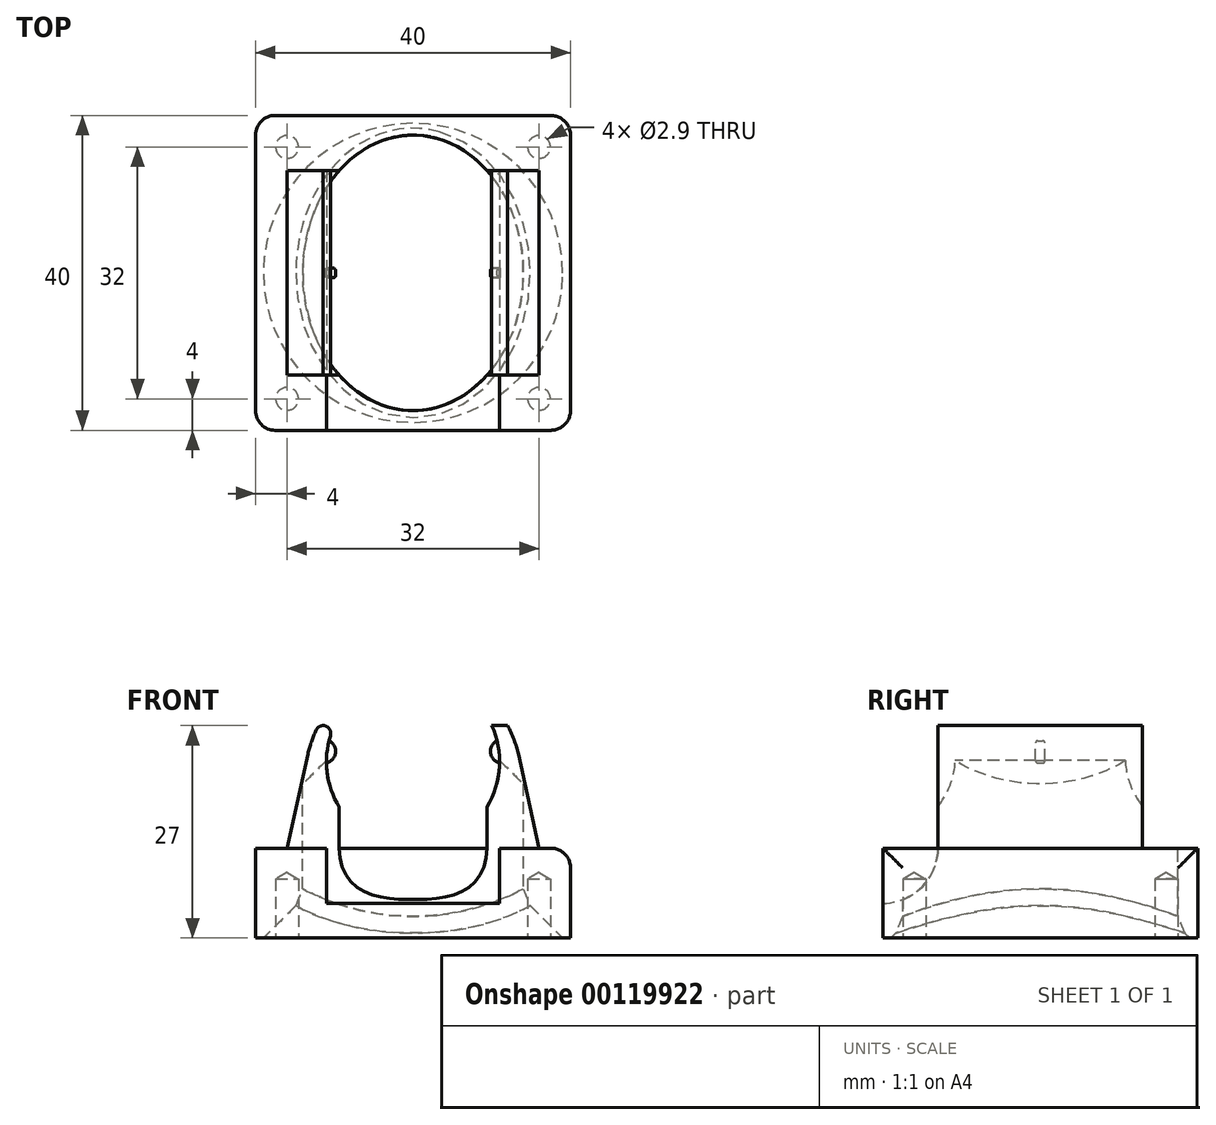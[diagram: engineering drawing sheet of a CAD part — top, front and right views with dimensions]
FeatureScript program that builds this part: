
annotation { "Feature Type Name" : "Feature", "Feature Type Description" : "" }
export const myFeature = defineFeature(function(context is Context, id is Id, definition is map)
    precondition{}
    {
        {
            var Q0;
            Q0=qCreatedBy(makeId("Top.planeOp"),FACE);
            var sketch = newSketch(context, id + "F0", { "sketchPlane" : qUnion([Q0])});
            skLineSegment(sketch, "E0.bottom", {"start": v(20, 20) * mm, "end": v(-20, 20) * mm});
            skLineSegment(sketch, "E0.top", {"start": v(20, -20) * mm, "end": v(-20, -20) * mm});
            skLineSegment(sketch, "E0.left", {"start": v(20, 20) * mm, "end": v(20, -20) * mm});
            skLineSegment(sketch, "E0.right", {"start": v(-20, 20) * mm, "end": v(-20, -20) * mm});
            skPoint(sketch, "E0.middle", {"position": v(0, 0) * mm});
            skSolve(sketch);
        }
        {
            var Q0;
            Q0 = qSketchRegion(id + "F0", true);
            extrude(context, id + "F1", {"entities" : qUnion([Q0]), "depth" : 27 * mm});
        }
        {
            var Q0;
            Q0=makeQuery(id+"F1.opExtrude","SWEPT_FACE",FACE,{"disambiguationData":[OSD([sQuery(id+"F0.wireOp",EDGE,"E0.top")])]});
            var sketch = newSketch(context, id + "F2", { "sketchPlane" : qUnion([Q0])});
            skCircle(sketch, "E1", {"center": v(0, 22.42) * mm, "radius": 11 * mm});
            skLineSegment(sketch, "E2", {"start": v(-10, 27) * mm, "end": v(10, 27) * mm, "construction": true});
            skArc(sketch, "E3", {"start": v(13.37, 23.36) * mm, "mid": v(0, 34.1) * mm, "end": v(-13.37, 23.36) * mm});
            skLineSegment(sketch, "E4", {"start": v(10, 27) * mm, "end": v(12, 27) * mm, "construction": true});
            skLineSegment(sketch, "E5", {"start": v(-20, 11.42) * mm, "end": v(20, 11.42) * mm, "construction": true});
            skLineSegment(sketch, "E6", {"start": v(-16, 11.42) * mm, "end": v(-13.37, 23.36) * mm});
            skLineSegment(sketch, "E7", {"start": v(16, 11.42) * mm, "end": v(13.37, 23.36) * mm});
            skLineSegment(sketch, "E8", {"start": v(-16, 11.42) * mm, "end": v(-20, 11.42) * mm});
            skLineSegment(sketch, "E9", {"start": v(-20, 27) * mm, "end": v(20, 27) * mm});
            skLineSegment(sketch, "E10", {"start": v(20, 27) * mm, "end": v(20, 11.42) * mm});
            skLineSegment(sketch, "E11", {"start": v(20, 11.42) * mm, "end": v(16, 11.42) * mm});
            skLineSegment(sketch, "E12", {"start": v(-20, 11.42) * mm, "end": v(-20, 27) * mm});
            skSolve(sketch);
        }
        {
            var Q0;
            {var subQ0=sQuery(id+"F2.wireOp",EDGE,"E1");var subQ1=makeQuery(id+"F1.opExtrude","CAP_EDGE",EDGE,{"disambiguationData":[OSD([sQuery(id+"F0.wireOp",EDGE,"E0.top")])],"isStart":false});var subQ2=makeQuery(id+"F2.imprint","INTERSECT",VERTEX,{"disambiguationData":[OD(0.0)],"derivedFrom":[subQ1,subQ0]});Q0=makeQuery(id+"F2.imprint","IMPRINT",FACE,{"disambiguationData":[TD([[makeQuery(id+"F2.imprint","IMPRINT",EDGE,{"disambiguationData":[TD([[subQ2,1.0]])],"derivedFrom":subQ0}),1.0]])]});}
            var Q1;
            Q1 = qSketchRegion(id + "F2", true);
            extrude(context, id + "F3", {"entities" : qUnion([Q0, Q1]), "operationType" : NewBodyOperationType.REMOVE, "endBound" : BoundingType.THROUGH_ALL, "oppositeDirection" : true, "depth" : 25 * mm});
        }
        {
            var Q0;
            Q0=makeQuery(id+"F1.opExtrude","SWEPT_FACE",FACE,{"disambiguationData":[OSD([sQuery(id+"F0.wireOp",EDGE,"E0.right")])]});
            var sketch = newSketch(context, id + "F4", { "sketchPlane" : qUnion([Q0])});
            skLineSegment(sketch, "E13.left", {"start": v(-13, 11.42) * mm, "end": v(-13, 27) * mm});
            skLineSegment(sketch, "E13.right", {"start": v(13, 11.42) * mm, "end": v(13, 27) * mm});
            skLineSegment(sketch, "E14", {"start": v(-13, 11.42) * mm, "end": v(-20, 11.42) * mm});
            skLineSegment(sketch, "E15", {"start": v(13, 11.42) * mm, "end": v(20, 11.42) * mm});
            skLineSegment(sketch, "E16", {"start": v(-20, 11.42) * mm, "end": v(-20, 27) * mm});
            skLineSegment(sketch, "E17", {"start": v(-20, 27) * mm, "end": v(-13, 27) * mm});
            skLineSegment(sketch, "E18", {"start": v(13, 27) * mm, "end": v(20, 27) * mm});
            skLineSegment(sketch, "E19", {"start": v(20, 27) * mm, "end": v(20, 11.42) * mm});
            skSolve(sketch);
        }
        {
            var Q0;
            Q0 = qSketchRegion(id + "F4", true);
            extrude(context, id + "F5", {"entities" : qUnion([Q0]), "operationType" : NewBodyOperationType.REMOVE, "endBound" : BoundingType.THROUGH_ALL, "oppositeDirection" : true, "depth" : 25 * mm});
        }
        {
            var Q0;
            Q0=makeQuery(id+"F1.opExtrude","CAP_FACE",FACE,{"disambiguationData":[OSD([sQuery(id+"F0.wireOp",EDGE,"E0.bottom"),sQuery(id+"F0.wireOp",EDGE,"E0.top"),sQuery(id+"F0.wireOp",EDGE,"E0.left"),sQuery(id+"F0.wireOp",EDGE,"E0.right")])],"isStart":true});
            var sketch = newSketch(context, id + "F6", { "sketchPlane" : qUnion([Q0])});
            skCircle(sketch, "E20", {"center": v(0, 0) * mm, "radius": 19 * mm});
            skSolve(sketch);
        }
        {
            var Q0;
            Q0=makeQuery(id+"F6.imprint","IMPRINT",FACE,{"disambiguationData":[TD([[makeQuery(id+"F6.imprint","IMPRINT",EDGE,{"derivedFrom":sQuery(id+"F6.wireOp",EDGE,"E20")}),1.0]])]});
            var Q1;
            Q1=sQuery(id+"F6.wireOp",EDGE,"E20");
            extrude(context, id + "F7", {"entities" : qUnion([Q0]), "operationType" : NewBodyOperationType.REMOVE, "surfaceEntities" : qUnion([Q1]), "oppositeDirection" : true, "depth" : 9 * mm});
        }
        {
            var Q0;
            Q0=makeQuery(id+"F7.boolean.opBoolean","COPY",FACE,{"derivedFrom":makeQuery(id+"F7.opExtrude","CAP_FACE",FACE,{"disambiguationData":[OSD([sQuery(id+"F6.wireOp",EDGE,"E20")])],"isStart":false})});
            var sketch = newSketch(context, id + "F8", { "sketchPlane" : qUnion([Q0])});
            skEllipse(sketch, "E21", {"center": v(0, 0) * mm, "majorRadius": 17.5 * mm, "minorRadius": 14 * mm, "majorAxis": v(0, 1)});
            skSolve(sketch);
        }
        {
            var Q0;
            Q0 = qSketchRegion(id + "F8", true);
            extrude(context, id + "F9", {"entities" : qUnion([Q0]), "operationType" : NewBodyOperationType.REMOVE, "oppositeDirection" : true, "depth" : 9.1 * mm});
        }
        {
            var Q0;
            Q0=makeQuery(id+"F5.boolean.opBoolean","INTERSECT",EDGE,{"derivedFrom":[makeQuery(id+"F5.opExtrude","SWEPT_FACE",FACE,{"disambiguationData":[OSD([sQuery(id+"F4.wireOp",EDGE,"E14")])]}),makeQuery(id+"F5.opExtrude","SWEPT_FACE",FACE,{"disambiguationData":[OSD([sQuery(id+"F4.wireOp",EDGE,"E15")])]})]});
            var Q1;
            Q1=makeQuery(id+"F3.boolean.opBoolean","COPY",EDGE,{"derivedFrom":makeQuery(id+"F3.opExtrude","SWEPT_EDGE",EDGE,{"disambiguationData":[OSD([sQuery(id+"F0.wireOp",EDGE,"E0.top"),sQuery(id+"F0.wireOp",EDGE,"E0.right"),sQuery(id+"F2.wireOp",EDGE,"E8"),sQuery(id+"F2.wireOp",EDGE,"E12")])]})});
            var Q2;
            Q2=makeQuery(id+"F5.boolean.opBoolean","MERGE",EDGE,{"derivedFrom":[makeQuery(id+"F3.boolean.opBoolean","COPY",EDGE,{"derivedFrom":makeQuery(id+"F3.opExtrude","CAP_EDGE",EDGE,{"disambiguationData":[OSD([sQuery(id+"F2.wireOp",EDGE,"E8")])],"isStart":true})}),makeQuery(id+"F3.boolean.opBoolean","COPY",EDGE,{"derivedFrom":makeQuery(id+"F3.opExtrude","CAP_EDGE",EDGE,{"disambiguationData":[OSD([sQuery(id+"F2.wireOp",EDGE,"E11")])],"isStart":true})}),makeQuery(id+"F5.opExtrude","SWEPT_EDGE",EDGE,{"disambiguationData":[OSD([sQuery(id+"F0.wireOp",EDGE,"E0.top"),sQuery(id+"F0.wireOp",EDGE,"E0.right"),sQuery(id+"F4.wireOp",EDGE,"E15"),sQuery(id+"F4.wireOp",EDGE,"E19")])]})]});
            var Q3;
            Q3=makeQuery(id+"F1.opExtrude","SWEPT_EDGE",EDGE,{"disambiguationData":[OSD([sQuery(id+"F0.wireOp",EDGE,"E0.top"),sQuery(id+"F0.wireOp",EDGE,"E0.right")])]});
            var Q4;
            Q4=makeQuery(id+"F1.opExtrude","SWEPT_EDGE",EDGE,{"disambiguationData":[OSD([sQuery(id+"F0.wireOp",EDGE,"E0.top"),sQuery(id+"F0.wireOp",EDGE,"E0.left")])]});
            var Q5;
            Q5=makeQuery(id+"F1.opExtrude","SWEPT_EDGE",EDGE,{"disambiguationData":[OSD([sQuery(id+"F0.wireOp",EDGE,"E0.bottom"),sQuery(id+"F0.wireOp",EDGE,"E0.left")])]});
            var Q6;
            Q6=makeQuery(id+"F1.opExtrude","SWEPT_EDGE",EDGE,{"disambiguationData":[OSD([sQuery(id+"F0.wireOp",EDGE,"E0.bottom"),sQuery(id+"F0.wireOp",EDGE,"E0.right")])]});
            var Q7;
            {var subQ0=sQuery(id+"F0.wireOp",EDGE,"E0.bottom");var subQ1=makeQuery(id+"F1.opExtrude","SWEPT_FACE",FACE,{"disambiguationData":[OSD([subQ0])]});Q7=makeQuery(id+"F5.boolean.opBoolean","MERGE",EDGE,{"derivedFrom":[makeQuery(id+"F3.boolean.opBoolean","INTERSECT",EDGE,{"derivedFrom":[subQ1,makeQuery(id+"F3.opExtrude","SWEPT_FACE",FACE,{"disambiguationData":[OSD([sQuery(id+"F2.wireOp",EDGE,"E8")])]})]}),makeQuery(id+"F3.boolean.opBoolean","INTERSECT",EDGE,{"derivedFrom":[subQ1,makeQuery(id+"F3.opExtrude","SWEPT_FACE",FACE,{"disambiguationData":[OSD([sQuery(id+"F2.wireOp",EDGE,"E11")])]})]}),makeQuery(id+"F5.opExtrude","SWEPT_EDGE",EDGE,{"disambiguationData":[OSD([subQ0,sQuery(id+"F0.wireOp",EDGE,"E0.right"),sQuery(id+"F4.wireOp",EDGE,"E14"),sQuery(id+"F4.wireOp",EDGE,"E16")])]})]});}
            fillet(context, id + "F10", {"entities" : qUnion([Q0, Q1, Q2, Q3, Q4, Q5, Q6, Q7]), "radius" : 2.5 * mm, "allowEdgeOverflow" : false});
        }
        {
            var Q0;
            Q0=makeQuery(id+"F7.boolean.opBoolean","COPY",EDGE,{"derivedFrom":makeQuery(id+"F7.opExtrude","CAP_EDGE",EDGE,{"disambiguationData":[OSD([sQuery(id+"F6.wireOp",EDGE,"E20")])],"isStart":false})});
            chamfer(context, id + "F11", {"entities" : qUnion([Q0]), "width" : 9 * mm, "tangentPropagation" : true});
        }
        {
            var Q0;
            Q0=makeQuery(id+"F11.opChamfer","BLEND_EDGE",EDGE,{"blendedFrom":[makeQuery(id+"F7.boolean.opBoolean","COPY",EDGE,{"derivedFrom":makeQuery(id+"F7.opExtrude","CAP_EDGE",EDGE,{"disambiguationData":[OSD([sQuery(id+"F6.wireOp",EDGE,"E20")])],"isStart":false})}),makeQuery(id+"F9.boolean.opBoolean","COPY",FACE,{"derivedFrom":makeQuery(id+"F9.opExtrude","SWEPT_FACE",FACE,{"disambiguationData":[OSD([sQuery(id+"F8.wireOp",EDGE,"E21")])]})})],"blendedInto":[makeQuery(id+"F9.boolean.opBoolean","COPY",FACE,{"derivedFrom":makeQuery(id+"F9.opExtrude","SWEPT_FACE",FACE,{"disambiguationData":[OSD([sQuery(id+"F8.wireOp",EDGE,"E21")])]})})]});
            chamfer(context, id + "F12", {"entities" : qUnion([Q0]), "width" : 3 * mm, "tangentPropagation" : true});
        }
        {
            var Q0;
            Q0=makeQuery(id+"F1.opExtrude","CAP_FACE",FACE,{"disambiguationData":[OSD([sQuery(id+"F0.wireOp",EDGE,"E0.bottom"),sQuery(id+"F0.wireOp",EDGE,"E0.top"),sQuery(id+"F0.wireOp",EDGE,"E0.left"),sQuery(id+"F0.wireOp",EDGE,"E0.right")])],"isStart":true});
            var sketch = newSketch(context, id + "F13", { "sketchPlane" : qUnion([Q0])});
            skLineSegment(sketch, "E22.bottom", {"start": v(16, -16) * mm, "end": v(-16, -16) * mm, "construction": true});
            skLineSegment(sketch, "E22.top", {"start": v(16, 16) * mm, "end": v(-16, 16) * mm, "construction": true});
            skLineSegment(sketch, "E22.left", {"start": v(16, -16) * mm, "end": v(16, 16) * mm, "construction": true});
            skLineSegment(sketch, "E22.right", {"start": v(-16, -16) * mm, "end": v(-16, 16) * mm, "construction": true});
            skPoint(sketch, "E22.middle", {"position": v(0, 0) * mm});
            skSolve(sketch);
        }
        {
            var Q0;
            Q0=sQuery(id+"F13.wireOp",VERTEX,"E22.right.end");
            var Q1;
            Q1=sQuery(id+"F13.wireOp",VERTEX,"E22.left.end");
            var Q2;
            Q2=sQuery(id+"F13.wireOp",VERTEX,"E22.left.start");
            var Q3;
            Q3=sQuery(id+"F13.wireOp",VERTEX,"E22.right.start");
            var Q4;
            Q4=makeQuery(id+"F1.opExtrude","SWEPT_BODY",BODY,{"disambiguationData":[OSD([sQuery(id+"F0.wireOp",EDGE,"E0.bottom"),sQuery(id+"F0.wireOp",EDGE,"E0.top"),sQuery(id+"F0.wireOp",EDGE,"E0.left"),sQuery(id+"F0.wireOp",EDGE,"E0.right")])]});
            hole(context, id + "F14", {"style" : HoleStyle.SIMPLE, "endStyle" : HoleEndStyle.BLIND, "holeDiameter" : 2.9 * mm, "holeDepth" : 7.5 * mm, "locations" : qUnion([Q0, Q1, Q2, Q3]), "scope" : qUnion([Q4])});
        }
        {
            var Q0;
            Q0=makeQuery(id+"F9.boolean.opBoolean","INTERSECT",EDGE,{"disambiguationData":[OD(0.0)],"derivedFrom":[makeQuery(id+"F3.boolean.opBoolean","COPY",FACE,{"derivedFrom":makeQuery(id+"F3.opExtrude","SWEPT_FACE",FACE,{"disambiguationData":[OSD([sQuery(id+"F2.wireOp",EDGE,"E1")])]})}),makeQuery(id+"F9.opExtrude","CAP_FACE",FACE,{"disambiguationData":[OSD([sQuery(id+"F8.wireOp",EDGE,"E21")])],"isStart":false})]});
            var Q1;
            Q1=makeQuery(id+"F9.boolean.opBoolean","INTERSECT",EDGE,{"disambiguationData":[OD(1.0)],"derivedFrom":[makeQuery(id+"F3.boolean.opBoolean","COPY",FACE,{"derivedFrom":makeQuery(id+"F3.opExtrude","SWEPT_FACE",FACE,{"disambiguationData":[OSD([sQuery(id+"F2.wireOp",EDGE,"E1")])]})}),makeQuery(id+"F9.opExtrude","CAP_FACE",FACE,{"disambiguationData":[OSD([sQuery(id+"F8.wireOp",EDGE,"E21")])],"isStart":false})]});
            chamfer(context, id + "F15", {"entities" : qUnion([Q0, Q1]), "width" : 4.5 * mm, "tangentPropagation" : true});
        }
        {
            var Q0;
            Q0=makeQuery(id+"F10.opFillet","SPLIT",FACE,{"disambiguationData":[OD(1.0)],"derivedFrom":makeQuery(id+"F5.boolean.opBoolean","MERGE",FACE,{"derivedFrom":[makeQuery(id+"F3.boolean.opBoolean","COPY",FACE,{"derivedFrom":makeQuery(id+"F3.opExtrude","SWEPT_FACE",FACE,{"disambiguationData":[OSD([sQuery(id+"F2.wireOp",EDGE,"E8")])]})}),makeQuery(id+"F3.boolean.opBoolean","COPY",FACE,{"derivedFrom":makeQuery(id+"F3.opExtrude","SWEPT_FACE",FACE,{"disambiguationData":[OSD([sQuery(id+"F2.wireOp",EDGE,"E11")])]})}),makeQuery(id+"F5.opExtrude","SWEPT_FACE",FACE,{"disambiguationData":[OSD([sQuery(id+"F4.wireOp",EDGE,"E14")])]}),makeQuery(id+"F5.opExtrude","SWEPT_FACE",FACE,{"disambiguationData":[OSD([sQuery(id+"F4.wireOp",EDGE,"E15")])]})]})});
            var sketch = newSketch(context, id + "F16", { "sketchPlane" : qUnion([Q0])});
            skLineSegment(sketch, "E23.bottom", {"start": v(-11, -13) * mm, "end": v(11, -13) * mm});
            skLineSegment(sketch, "E23.top", {"start": v(-11, -20) * mm, "end": v(11, -20) * mm});
            skLineSegment(sketch, "E23.left", {"start": v(-11, -13) * mm, "end": v(-11, -20) * mm});
            skLineSegment(sketch, "E23.right", {"start": v(11, -13) * mm, "end": v(11, -20) * mm});
            skLineSegment(sketch, "E24", {"start": v(0, -13) * mm, "end": v(0, -20) * mm, "construction": true});
            skSolve(sketch);
        }
        {
            var Q0;
            {var subQ0=sQuery(id+"F2.wireOp",EDGE,"E9");var subQ1=sQuery(id+"F2.wireOp",EDGE,"E1");Q0=makeQuery(id+"F3.boolean.opBoolean","COPY",EDGE,{"derivedFrom":makeQuery(id+"F3.opExtrude","SWEPT_EDGE",EDGE,{"disambiguationData":[OSD([subQ1,subQ0]),TDD([makeQuery(id+"F2.imprint","INTERSECT",VERTEX,{"disambiguationData":[OD(0.0)],"derivedFrom":[subQ1,subQ0]})])]})});}
            var Q1;
            {var subQ0=sQuery(id+"F2.wireOp",EDGE,"E9");var subQ1=sQuery(id+"F2.wireOp",EDGE,"E3");Q1=makeQuery(id+"F3.boolean.opBoolean","COPY",EDGE,{"derivedFrom":makeQuery(id+"F3.opExtrude","SWEPT_EDGE",EDGE,{"disambiguationData":[OSD([subQ1,subQ0]),TDD([makeQuery(id+"F2.imprint","INTERSECT",VERTEX,{"disambiguationData":[OD(0.0)],"derivedFrom":[subQ1,subQ0]})]),ownerDisambiguation([makeQuery(id+"F3.opExtrude","SWEPT_BODY",BODY,{"disambiguationData":[OSD([subQ1,sQuery(id+"F2.wireOp",EDGE,"E7"),subQ0,sQuery(id+"F2.wireOp",EDGE,"E10"),sQuery(id+"F2.wireOp",EDGE,"E11")])]})])]})});}
            var Q2;
            {var subQ0=sQuery(id+"F2.wireOp",EDGE,"E9");var subQ1=sQuery(id+"F2.wireOp",EDGE,"E1");Q2=makeQuery(id+"F3.boolean.opBoolean","COPY",EDGE,{"derivedFrom":makeQuery(id+"F3.opExtrude","SWEPT_EDGE",EDGE,{"disambiguationData":[OSD([subQ1,subQ0]),TDD([makeQuery(id+"F2.imprint","INTERSECT",VERTEX,{"disambiguationData":[OD(1.0)],"derivedFrom":[subQ1,subQ0]})])]})});}
            var Q3;
            {var subQ0=sQuery(id+"F2.wireOp",EDGE,"E9");var subQ1=sQuery(id+"F2.wireOp",EDGE,"E3");Q3=makeQuery(id+"F3.boolean.opBoolean","COPY",EDGE,{"derivedFrom":makeQuery(id+"F3.opExtrude","SWEPT_EDGE",EDGE,{"disambiguationData":[OSD([subQ1,subQ0]),TDD([makeQuery(id+"F2.imprint","INTERSECT",VERTEX,{"disambiguationData":[OD(1.0)],"derivedFrom":[subQ1,subQ0]})]),ownerDisambiguation([makeQuery(id+"F3.opExtrude","SWEPT_BODY",BODY,{"disambiguationData":[OSD([subQ1,sQuery(id+"F2.wireOp",EDGE,"E6"),sQuery(id+"F2.wireOp",EDGE,"E8"),subQ0,sQuery(id+"F2.wireOp",EDGE,"E12")])]})])]})});}
            fillet(context, id + "F17", {"entities" : qUnion([Q0, Q1, Q2, Q3]), "radius" : 1 * mm, "tangentPropagation" : true, "allowEdgeOverflow" : false});
        }
        {
            var Q0;
            Q0=qCreatedBy(makeId("Front.planeOp"),FACE);
            var sketch = newSketch(context, id + "F18", { "sketchPlane" : qUnion([Q0])});
            skArc(sketch, "E25", {"start": v(10.68, 25.07) * mm, "mid": v(9.85, 23.54) * mm, "end": v(11, 22.24) * mm});
            skLineSegment(sketch, "E26", {"start": v(10.68, 25.07) * mm, "end": v(11.2, 23.72) * mm});
            skLineSegment(sketch, "E27", {"start": v(11.2, 23.72) * mm, "end": v(11, 22.24) * mm});
            skLineSegment(sketch, "E28.MirrorCS", {"start": v(-11.2, 23.72) * mm, "end": v(-11, 22.24) * mm});
            skLineSegment(sketch, "E29.MirrorCS", {"start": v(-10.68, 25.07) * mm, "end": v(-11.2, 23.72) * mm});
            skArc(sketch, "E30.MirrorCS", {"start": v(-10.68, 25.07) * mm, "mid": v(-9.85, 23.54) * mm, "end": v(-11, 22.24) * mm});
            skSolve(sketch);
        }
        {
            var Q0;
            Q0 = qSketchRegion(id + "F18", true);
            extrude(context, id + "F19", {"entities" : qUnion([Q0]), "operationType" : NewBodyOperationType.ADD, "depth" : .6 * mm});
        }
        {
            var Q0;
            Q0 = qSketchRegion(id + "F18", true);
            extrude(context, id + "F20", {"entities" : qUnion([Q0]), "operationType" : NewBodyOperationType.ADD, "oppositeDirection" : true, "depth" : .6 * mm});
        }
        {
            var Q0;
            Q0=makeQuery(id+"F20.opExtrude","CAP_EDGE",EDGE,{"disambiguationData":[OSD([sQuery(id+"F18.wireOp",EDGE,"E25")])],"isStart":false});
            var Q1;
            Q1=makeQuery(id+"F19.opExtrude","CAP_EDGE",EDGE,{"disambiguationData":[OSD([sQuery(id+"F18.wireOp",EDGE,"E25")])],"isStart":false});
            var Q2;
            Q2=makeQuery(id+"F20.opExtrude","CAP_EDGE",EDGE,{"disambiguationData":[OSD([sQuery(id+"F18.wireOp",EDGE,"E30.MirrorCS")])],"isStart":false});
            var Q3;
            Q3=makeQuery(id+"F19.opExtrude","CAP_EDGE",EDGE,{"disambiguationData":[OSD([sQuery(id+"F18.wireOp",EDGE,"E30.MirrorCS")])],"isStart":false});
            fillet(context, id + "F21", {"entities" : qUnion([Q0, Q1, Q2, Q3]), "radius" : 0.3 * mm, "tangentPropagation" : true, "allowEdgeOverflow" : false});
        }
        {
            var Q0;
            {var subQ2=sQuery(id+"F16.wireOp",EDGE,"E23.top");Q0=makeQuery(id+"F16.imprint","IMPRINT",FACE,{"disambiguationData":[TD([[makeQuery(id+"F16.imprint","IMPRINT",EDGE,{"derivedFrom":subQ2}),1.0]])]});}
            var Q1;
            Q1 = qSketchRegion(id + "F16", true);
            var Q2;
            Q2=sQuery(id+"F16.wireOp",EDGE,"E23.top");
            revolve(context, id + "F22", {"operationType" : NewBodyOperationType.REMOVE, "entities" : qUnion([Q0, Q1]), "axis" : qUnion([Q2]), "revolveType" : RevolveType.FULL, "oppositeDirection" : true});
        }
    });
